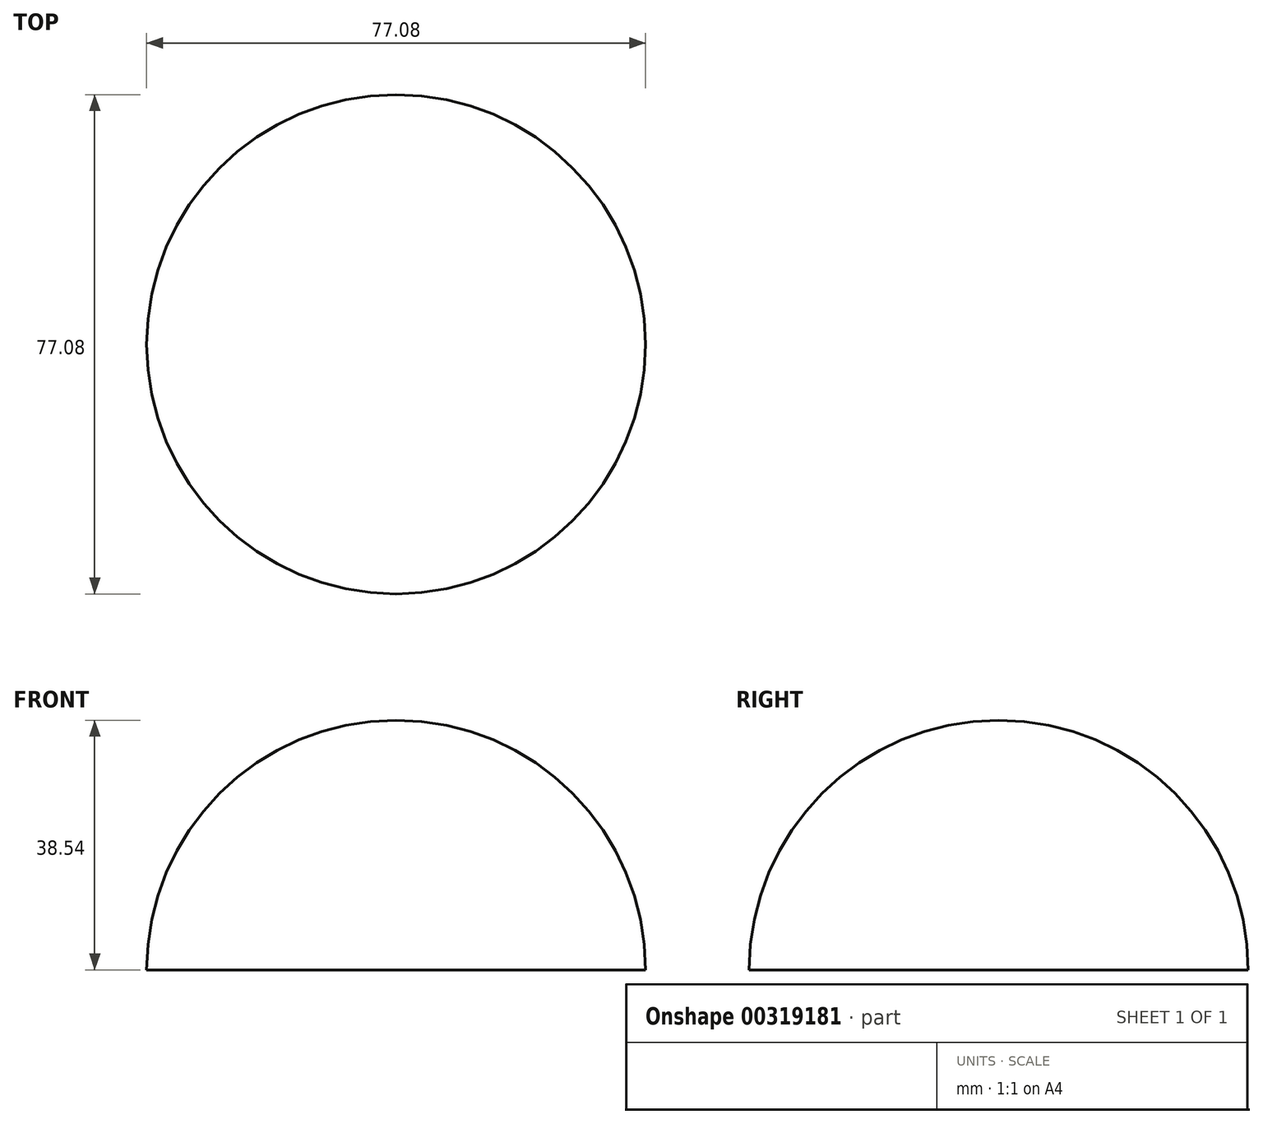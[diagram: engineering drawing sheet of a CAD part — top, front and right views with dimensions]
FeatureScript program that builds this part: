
annotation { "Feature Type Name" : "Feature", "Feature Type Description" : "" }
export const myFeature = defineFeature(function(context is Context, id is Id, definition is map)
    precondition{}
    {
        {
            var Q0;
            Q0=qCreatedBy(makeId("Front.planeOp"),FACE);
            var sketch = newSketch(context, id + "F0", { "sketchPlane" : qUnion([Q0])});
            skCircle(sketch, "E0", {"center": v(0, 0) * mm, "radius": 38.54 * mm});
            skLineSegment(sketch, "E1", {"start": v(0, 0) * mm, "end": v(-38.54, 0) * mm});
            skLineSegment(sketch, "E2", {"start": v(0, 0) * mm, "end": v(38.54, 0) * mm});
            skLineSegment(sketch, "E3", {"start": v(33.52, 19) * mm, "end": v(48.93, 35.11) * mm});
            skSolve(sketch);
        }
        {
            var Q0;
            {var subQ0=sQuery(id+"F0.wireOp",EDGE,"E1");Q0=makeQuery(id+"F0.imprint","IMPRINT",FACE,{"disambiguationData":[TD([[makeQuery(id+"F0.imprint","IMPRINT",EDGE,{"derivedFrom":subQ0}),-1.0]])]});}
            var Q1;
            Q1=sQuery(id+"F0.wireOp",EDGE,"E2");
            revolve(context, id + "F1", {"entities" : qUnion([Q0]), "axis" : qUnion([Q1]), "revolveType" : RevolveType.SYMMETRIC, "angle" : 180 * degree});
        }
    });
